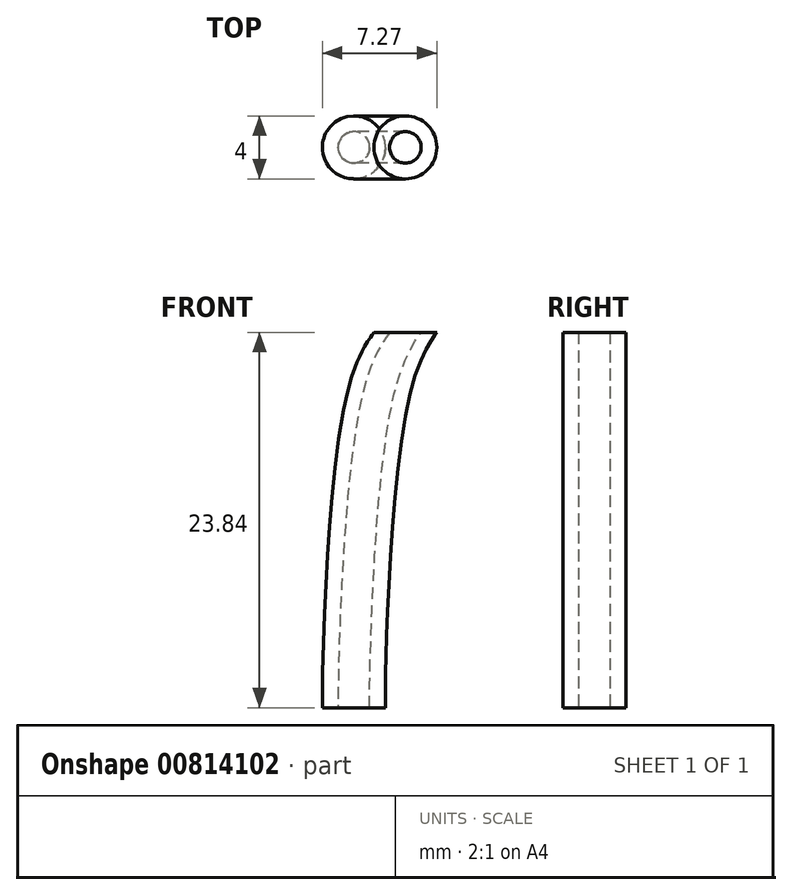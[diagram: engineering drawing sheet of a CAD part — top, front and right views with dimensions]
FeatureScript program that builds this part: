
annotation { "Feature Type Name" : "Feature", "Feature Type Description" : "" }
export const myFeature = defineFeature(function(context is Context, id is Id, definition is map)
    precondition{}
    {
        {
            var Q0;
            Q0=qCreatedBy(makeId("Top.planeOp"),FACE);
            var sketch = newSketch(context, id + "F0", { "sketchPlane" : qUnion([Q0])});
            skCircle(sketch, "E0", {"center": v(0, 0) * mm, "radius": 1 * mm});
            skCircle(sketch, "E1", {"center": v(0, 0) * mm, "radius": 2 * mm});
            skSolve(sketch);
        }
        {
            var Q0;
            Q0=qCreatedBy(makeId("Front.planeOp"),FACE);
            var sketch = newSketch(context, id + "F1", { "sketchPlane" : qUnion([Q0])});
            skFitSpline(sketch, "E2", {"points": [v(0, 0) * mm, v(0, 0.84) * mm, v(0, 1.3) * mm, v(1.64, 20.27) * mm, v(3.27, 23.84) * mm], "startDerivative": vector(0.02, 3.42) * mm, "endDerivative": vector(1.79, 3.15) * mm});
            skSolve(sketch);
        }
        {
            var Q0;
            Q0=makeQuery(id+"F0.imprint","IMPRINT",FACE,{"disambiguationData":[TD([[makeQuery(id+"F0.imprint","IMPRINT",EDGE,{"derivedFrom":sQuery(id+"F0.wireOp",EDGE,"E0")}),-1.0]])]});
            var Q1;
            Q1=sQuery(id+"F1.wireOp",EDGE,"E2");
            sweep(context, id + "F2", {"profiles" : qUnion([Q0]), "path" : qUnion([Q1]), "keepProfileOrientation" : true});
        }
    });
